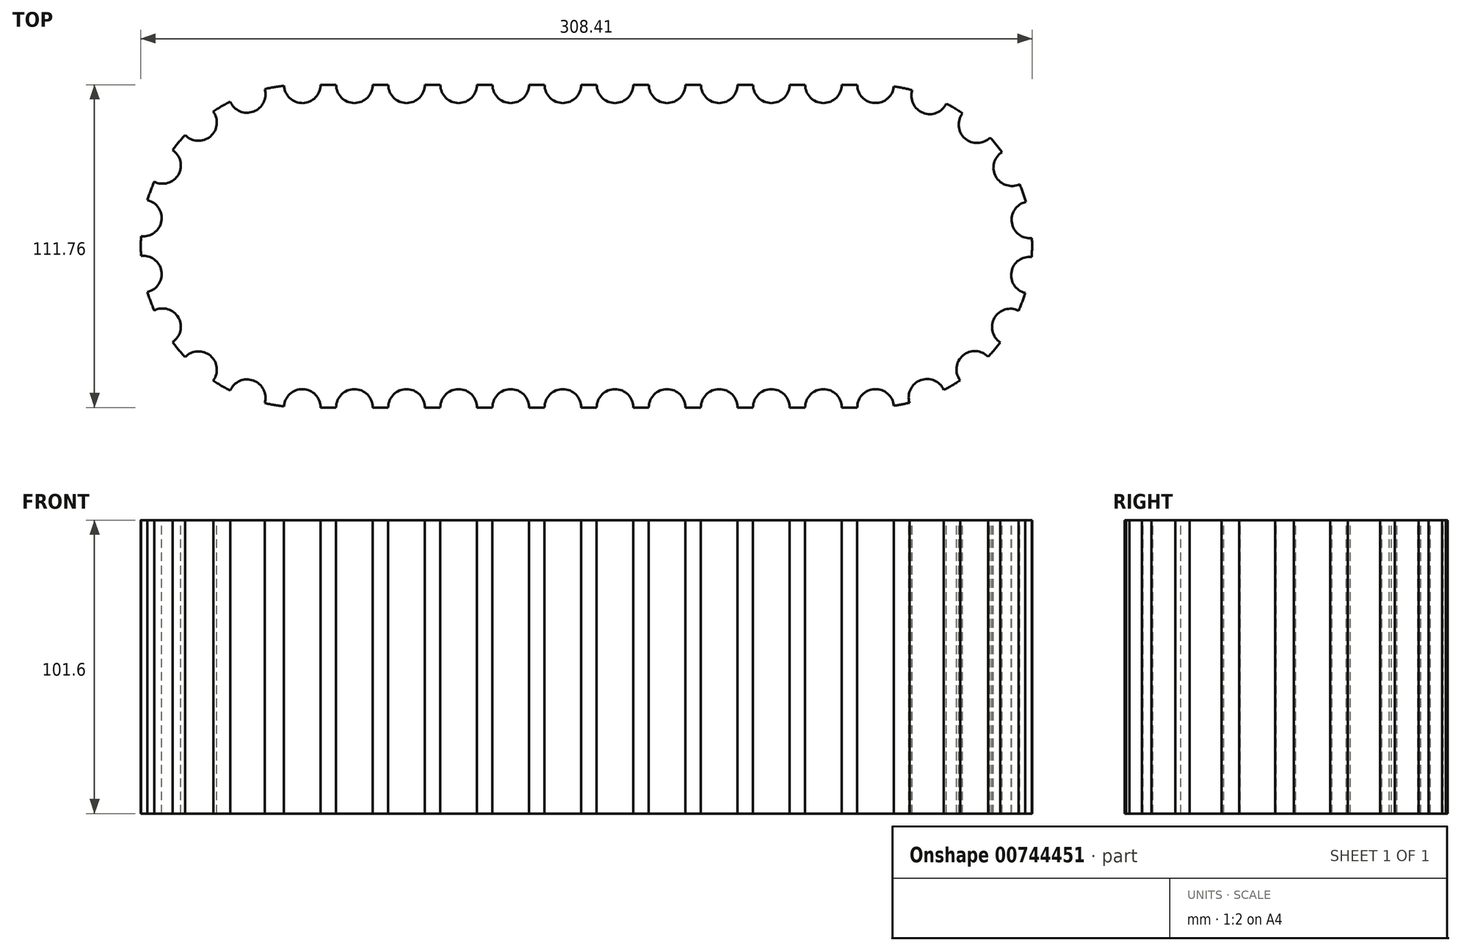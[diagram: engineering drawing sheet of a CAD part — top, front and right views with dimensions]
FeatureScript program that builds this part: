
annotation { "Feature Type Name" : "Feature", "Feature Type Description" : "" }
export const myFeature = defineFeature(function(context is Context, id is Id, definition is map)
    precondition{}
    {
        {
            var Q0;
            Q0=qCreatedBy(makeId("Top.planeOp"),FACE);
            var sketch = newSketch(context, id + "F0", { "sketchPlane" : qUnion([Q0])});
            skArc(sketch, "E0", {"start": v(-196.65, 55.88) * mm, "mid": v(-252.53, 0) * mm, "end": v(-196.65, -55.88) * mm});
            skArc(sketch, "E1", {"start": v(0, -55.88) * mm, "mid": v(55.88, 0) * mm, "end": v(0, 55.88) * mm});
            skLineSegment(sketch, "E2", {"start": v(-196.65, 55.88) * mm, "end": v(0, 55.88) * mm});
            skLineSegment(sketch, "E3", {"start": v(-196.65, -55.88) * mm, "end": v(0, -55.88) * mm});
            skSolve(sketch);
        }
        {
            var Q0;
            Q0=makeQuery(id+"F0.imprint","IMPRINT",FACE,{"disambiguationData":[TD([[makeQuery(id+"F0.imprint","IMPRINT",EDGE,{"derivedFrom":sQuery(id+"F0.wireOp",EDGE,"E0")}),1.0]])]});
            extrude(context, id + "F1", {"entities" : qUnion([Q0]), "depth" : 101.6 * mm});
        }
        {
            var Q0;
            Q0=makeQuery(id+"F1.opExtrude","CAP_FACE",FACE,{"disambiguationData":[OSD([sQuery(id+"F0.wireOp",EDGE,"E0"),sQuery(id+"F0.wireOp",EDGE,"E1"),sQuery(id+"F0.wireOp",EDGE,"E2"),sQuery(id+"F0.wireOp",EDGE,"E3")])],"isStart":false});
            var sketch = newSketch(context, id + "F2", { "sketchPlane" : qUnion([Q0])});
            skCircle(sketch, "E4", {"center": v(-196.65, 55.88) * mm, "radius": 6.35 * mm});
            skCircle(sketch, "E5.1.0.0", {"center": v(-178.61, 55.88) * mm, "radius": 6.35 * mm});
            skCircle(sketch, "E5.2.0.0", {"center": v(-160.58, 55.88) * mm, "radius": 6.35 * mm});
            skCircle(sketch, "E5.3.0.0", {"center": v(-142.54, 55.88) * mm, "radius": 6.35 * mm});
            skCircle(sketch, "E5.4.0.0", {"center": v(-124.51, 55.88) * mm, "radius": 6.35 * mm});
            skCircle(sketch, "E5.5.0.0", {"center": v(-106.48, 55.88) * mm, "radius": 6.35 * mm});
            skCircle(sketch, "E5.6.0.0", {"center": v(-88.44, 55.88) * mm, "radius": 6.35 * mm});
            skCircle(sketch, "E5.7.0.0", {"center": v(-70.4, 55.88) * mm, "radius": 6.35 * mm});
            skCircle(sketch, "E5.8.0.0", {"center": v(-52.37, 55.88) * mm, "radius": 6.35 * mm});
            skCircle(sketch, "E5.9.0.0", {"center": v(-34.34, 55.88) * mm, "radius": 6.35 * mm});
            skCircle(sketch, "E5.10.0.0", {"center": v(-16.3, 55.88) * mm, "radius": 6.35 * mm});
            skCircle(sketch, "E5.11.0.0", {"center": v(1.73, 55.88) * mm, "radius": 6.35 * mm});
            skLineSegment(sketch, "E5.direction1", {"start": v(-196.65, 55.88) * mm, "end": v(-178.61, 55.88) * mm, "construction": true});
            skCircle(sketch, "E6", {"center": v(-196.65, -55.88) * mm, "radius": 6.35 * mm});
            skCircle(sketch, "E7.1.0.0", {"center": v(-178.61, -55.88) * mm, "radius": 6.35 * mm});
            skCircle(sketch, "E7.2.0.0", {"center": v(-160.58, -55.88) * mm, "radius": 6.35 * mm});
            skCircle(sketch, "E7.3.0.0", {"center": v(-142.54, -55.88) * mm, "radius": 6.35 * mm});
            skCircle(sketch, "E7.4.0.0", {"center": v(-124.51, -55.88) * mm, "radius": 6.35 * mm});
            skCircle(sketch, "E7.5.0.0", {"center": v(-106.48, -55.88) * mm, "radius": 6.35 * mm});
            skCircle(sketch, "E7.6.0.0", {"center": v(-88.44, -55.88) * mm, "radius": 6.35 * mm});
            skCircle(sketch, "E7.7.0.0", {"center": v(-70.4, -55.88) * mm, "radius": 6.35 * mm});
            skCircle(sketch, "E7.8.0.0", {"center": v(-52.37, -55.88) * mm, "radius": 6.35 * mm});
            skCircle(sketch, "E7.9.0.0", {"center": v(-34.34, -55.88) * mm, "radius": 6.35 * mm});
            skCircle(sketch, "E7.10.0.0", {"center": v(-16.3, -55.88) * mm, "radius": 6.35 * mm});
            skCircle(sketch, "E7.11.0.0", {"center": v(1.73, -55.88) * mm, "radius": 6.35 * mm});
            skLineSegment(sketch, "E7.direction1", {"start": v(-196.65, -55.88) * mm, "end": v(-178.61, -55.88) * mm, "construction": true});
            skCircle(sketch, "E8.1.0", {"center": v(-215.76, 52.51) * mm, "radius": 6.35 * mm});
            skCircle(sketch, "E8.2.0", {"center": v(-232.57, 42.8) * mm, "radius": 6.35 * mm});
            skCircle(sketch, "E8.3.0", {"center": v(-245.04, 27.94) * mm, "radius": 6.35 * mm});
            skCircle(sketch, "E8.4.0", {"center": v(-251.68, 9.7) * mm, "radius": 6.35 * mm});
            skCircle(sketch, "E8.5.0", {"center": v(-251.68, -9.7) * mm, "radius": 6.35 * mm});
            skCircle(sketch, "E8.6.0", {"center": v(-245.04, -27.94) * mm, "radius": 6.35 * mm});
            skCircle(sketch, "E8.7.0", {"center": v(-232.57, -42.8) * mm, "radius": 6.35 * mm});
            skCircle(sketch, "E8.8.0", {"center": v(-215.76, -52.51) * mm, "radius": 6.35 * mm});
            skPoint(sketch, "E8.center", {"position": v(-196.65, 0) * mm});
            skLineSegment(sketch, "E8.anchor1", {"start": v(-196.65, 0) * mm, "end": v(-196.65, 55.88) * mm, "construction": true});
            skLineSegment(sketch, "E8.anchor2", {"start": v(-196.65, 0) * mm, "end": v(-196.65, -55.88) * mm, "construction": true});
            skCircle(sketch, "E9.1.0", {"center": v(20.48, 52.02) * mm, "radius": 6.35 * mm});
            skCircle(sketch, "E9.2.0", {"center": v(36.84, 42.06) * mm, "radius": 6.35 * mm});
            skCircle(sketch, "E9.3.0", {"center": v(48.87, 27.16) * mm, "radius": 6.35 * mm});
            skCircle(sketch, "E9.4.0", {"center": v(55.17, 9.07) * mm, "radius": 6.35 * mm});
            skCircle(sketch, "E9.5.0", {"center": v(55, -10.07) * mm, "radius": 6.35 * mm});
            skCircle(sketch, "E9.6.0", {"center": v(48.37, -28.04) * mm, "radius": 6.35 * mm});
            skCircle(sketch, "E9.7.0", {"center": v(36.07, -42.72) * mm, "radius": 6.35 * mm});
            skCircle(sketch, "E9.8.0", {"center": v(19.53, -52.38) * mm, "radius": 6.35 * mm});
            skArc(sketch, "E9.9.0", {"start": v(1.08, -49.56) * mm, "mid": v(0.86, -49.55) * mm, "end": v(0.63, -49.55) * mm});
            skPoint(sketch, "E9.center", {"position": v(0, 0) * mm});
            skLineSegment(sketch, "E9.anchor2", {"start": v(0.63, -49.55) * mm, "end": v(0.63, -49.63) * mm, "construction": true});
            skSolve(sketch);
        }
        {
            var Q0;
            Q0=qSketchRegion(id+"F2",true);
            extrude(context, id + "F3", {"entities" : qUnion([Q0]), "operationType" : NewBodyOperationType.REMOVE, "endBound" : BoundingType.THROUGH_ALL, "oppositeDirection" : true, "depth" : 25.4 * mm});
        }
    });
